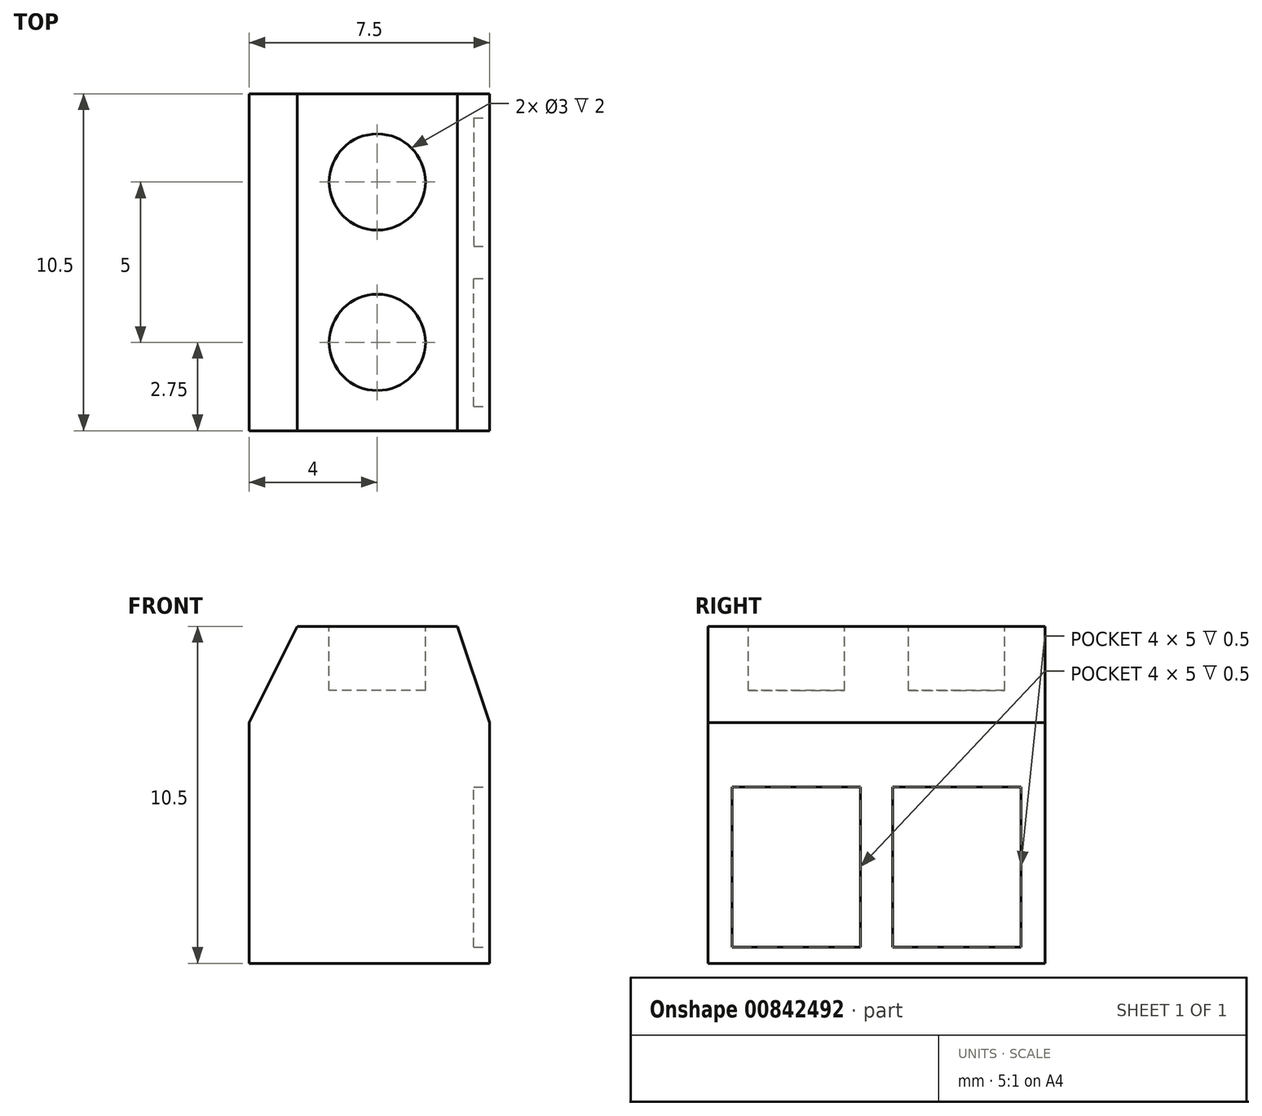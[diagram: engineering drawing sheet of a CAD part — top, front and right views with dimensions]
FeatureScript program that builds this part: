
annotation { "Feature Type Name" : "Feature", "Feature Type Description" : "" }
export const myFeature = defineFeature(function(context is Context, id is Id, definition is map)
    precondition{}
    {
        {
            var Q0;
            Q0=qCreatedBy(makeId("Front.planeOp"),FACE);
            var sketch = newSketch(context, id + "F0", { "sketchPlane" : qUnion([Q0])});
            skLineSegment(sketch, "E0.bottom", {"start": v(0, 0) * mm, "end": v(-7.5, 0) * mm});
            skLineSegment(sketch, "E0.top", {"start": v(0, 10.5) * mm, "end": v(-7.5, 10.5) * mm});
            skLineSegment(sketch, "E0.left", {"start": v(0, 0) * mm, "end": v(0, 10.5) * mm});
            skLineSegment(sketch, "E0.right", {"start": v(-7.5, 0) * mm, "end": v(-7.5, 10.5) * mm});
            skSolve(sketch);
        }
        {
            var Q0;
            Q0=qSketchRegion(id+"F0",true);
            extrude(context, id + "F1", {"entities" : qUnion([Q0]), "oppositeDirection" : true, "depth" : 10.5 * mm, "offsetDistance" : 25 * mm});
        }
        {
            var Q0;
            Q0=makeQuery(id+"F1.opExtrude","SWEPT_EDGE",EDGE,{"disambiguationData":[OSD([sQuery(id+"F0.wireOp",EDGE,"E0.top"),sQuery(id+"F0.wireOp",EDGE,"E0.right")])]});
            chamfer(context, id + "F2", {"entities" : qUnion([Q0]), "chamferType" : ChamferType.TWO_OFFSETS, "width1" : 1.5 * mm, "oppositeDirection" : false, "width2" : 3 * mm, "tangentPropagation" : true});
        }
        {
            var Q0;
            Q0=makeQuery(id+"F1.opExtrude","SWEPT_EDGE",EDGE,{"disambiguationData":[OSD([sQuery(id+"F0.wireOp",EDGE,"E0.top"),sQuery(id+"F0.wireOp",EDGE,"E0.left")])]});
            chamfer(context, id + "F3", {"entities" : qUnion([Q0]), "chamferType" : ChamferType.TWO_OFFSETS, "width1" : 3 * mm, "oppositeDirection" : false, "width2" : 1 * mm, "tangentPropagation" : true});
        }
        {
            var Q0;
            Q0=makeQuery(id+"F1.opExtrude","SWEPT_FACE",FACE,{"disambiguationData":[OSD([sQuery(id+"F0.wireOp",EDGE,"E0.top")])]});
            var sketch = newSketch(context, id + "F4", { "sketchPlane" : qUnion([Q0])});
            skCircle(sketch, "E1", {"center": v(-3.5, 2.75) * mm, "radius": 1.5 * mm});
            skLineSegment(sketch, "E2", {"start": v(-3.5, 10.5) * mm, "end": v(-3.5, 0) * mm, "construction": true});
            skCircle(sketch, "E3.0.1.0", {"center": v(-3.5, 7.75) * mm, "radius": 1.5 * mm});
            skLineSegment(sketch, "E3.direction2", {"start": v(-3.5, 2.75) * mm, "end": v(-3.5, 7.75) * mm, "construction": true});
            skLineSegment(sketch, "E4", {"start": v(-3.5, 5.25) * mm, "end": v(-5, 5.25) * mm, "construction": true});
            skLineSegment(sketch, "E5", {"start": v(-6, 5.25) * mm, "end": v(-1, 5.25) * mm, "construction": true});
            skSolve(sketch);
        }
        {
            var Q0;
            Q0=qSketchRegion(id+"F4",true);
            extrude(context, id + "F5", {"entities" : qUnion([Q0]), "operationType" : NewBodyOperationType.REMOVE, "oppositeDirection" : true, "depth" : 2 * mm, "offsetDistance" : 25 * mm});
        }
        {
            var Q0;
            Q0=makeQuery(id+"F1.opExtrude","SWEPT_FACE",FACE,{"disambiguationData":[OSD([sQuery(id+"F0.wireOp",EDGE,"E0.left")])]});
            var sketch = newSketch(context, id + "F6", { "sketchPlane" : qUnion([Q0])});
            skLineSegment(sketch, "E6.bottom", {"start": v(0.75, 0.5) * mm, "end": v(4.75, 0.5) * mm});
            skLineSegment(sketch, "E6.top", {"start": v(0.75, 5.5) * mm, "end": v(4.75, 5.5) * mm});
            skLineSegment(sketch, "E6.left", {"start": v(0.75, 0.5) * mm, "end": v(0.75, 5.5) * mm});
            skLineSegment(sketch, "E6.right", {"start": v(4.75, 0.5) * mm, "end": v(4.75, 5.5) * mm});
            skLineSegment(sketch, "E7", {"start": v(5.25, 0) * mm, "end": v(5.25, 7.5) * mm, "construction": true});
            skLineSegment(sketch, "E8.MirrorCS", {"start": v(9.75, 5.5) * mm, "end": v(5.75, 5.5) * mm});
            skLineSegment(sketch, "E9.MirrorCS", {"start": v(5.75, 0.5) * mm, "end": v(5.75, 5.5) * mm});
            skLineSegment(sketch, "E10.MirrorCS", {"start": v(9.75, 0.5) * mm, "end": v(5.75, 0.5) * mm});
            skLineSegment(sketch, "E11.MirrorCS", {"start": v(9.75, 0.5) * mm, "end": v(9.75, 5.5) * mm});
            skSolve(sketch);
        }
        {
            var Q0;
            Q0=makeQuery(id+"F6.imprint","IMPRINT",FACE,{"disambiguationData":[TD([[makeQuery(id+"F6.imprint","IMPRINT",EDGE,{"derivedFrom":sQuery(id+"F6.wireOp",EDGE,"E6.bottom")}),1.0]])]});
            var Q1;
            Q1=makeQuery(id+"F6.imprint","IMPRINT",FACE,{"disambiguationData":[TD([[makeQuery(id+"F6.imprint","IMPRINT",EDGE,{"derivedFrom":sQuery(id+"F6.wireOp",EDGE,"E8.MirrorCS")}),1.0]])]});
            extrude(context, id + "F7", {"entities" : qUnion([Q0, Q1]), "operationType" : NewBodyOperationType.REMOVE, "oppositeDirection" : true, "depth" : 0.5 * mm, "offsetDistance" : 25 * mm});
        }
    });
